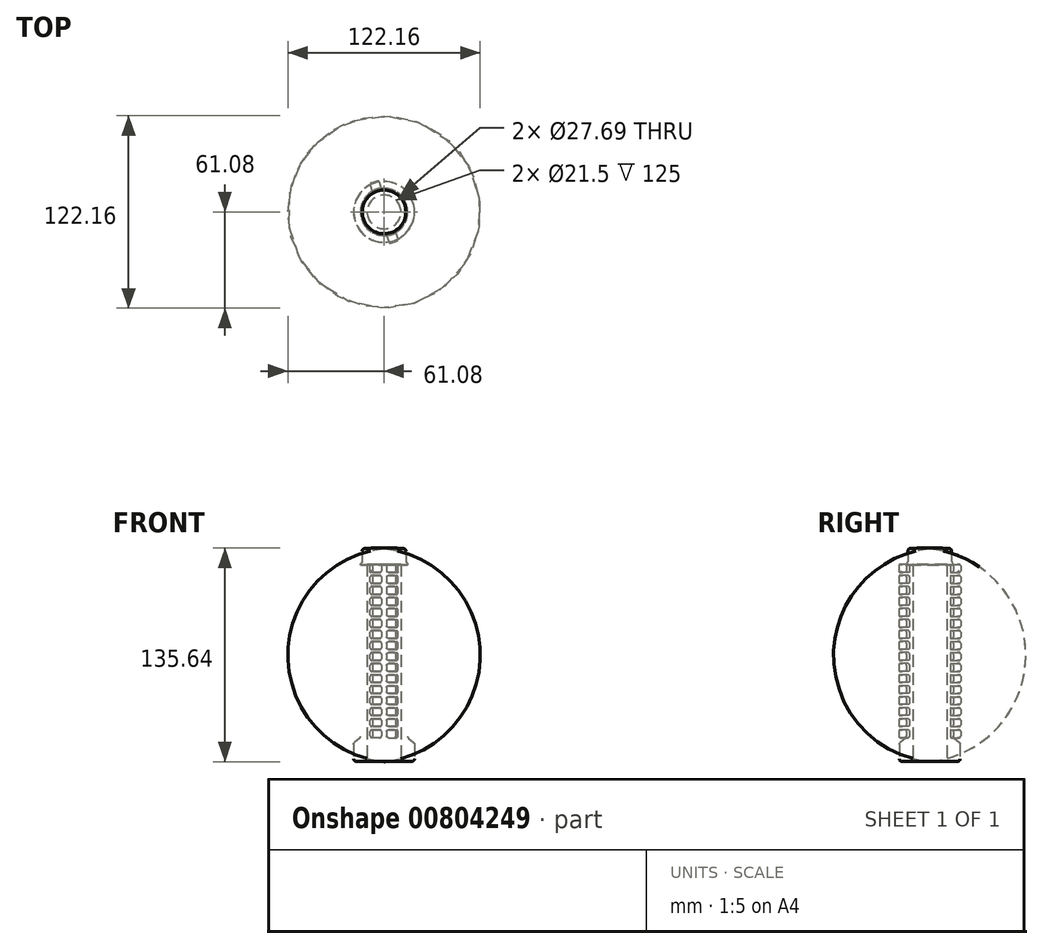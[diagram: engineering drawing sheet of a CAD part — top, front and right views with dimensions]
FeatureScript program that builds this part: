
annotation { "Feature Type Name" : "Feature", "Feature Type Description" : "" }
export const myFeature = defineFeature(function(context is Context, id is Id, definition is map)
    precondition{}
    {
        {
            var Q0;
            Q0=qCreatedBy(makeId("Front.planeOp"),FACE);
            var sketch = newSketch(context, id + "F0", { "sketchPlane" : qUnion([Q0])});
            skLineSegment(sketch, "E0", {"start": v(0, 0) * mm, "end": v(0, 125) * mm, "construction": true});
            skLineSegment(sketch, "E1", {"start": v(0, 135) * mm, "end": v(0, 125) * mm});
            skLineSegment(sketch, "E2", {"start": v(0, 125) * mm, "end": v(10.75, 125) * mm});
            skLineSegment(sketch, "E3", {"start": v(10.75, 125) * mm, "end": v(10.75, 0) * mm});
            skLineSegment(sketch, "E4", {"start": v(10.75, 0) * mm, "end": v(19.33, 0) * mm});
            skLineSegment(sketch, "E5", {"start": v(19.33, 0) * mm, "end": v(19.33, 11.37) * mm});
            skLineSegment(sketch, "E6", {"start": v(19.33, 11.37) * mm, "end": v(15, 15) * mm});
            skLineSegment(sketch, "E7", {"start": v(15, 15) * mm, "end": v(15, 125) * mm});
            skLineSegment(sketch, "E8", {"start": v(15, 125) * mm, "end": v(13.85, 127) * mm});
            skLineSegment(sketch, "E9", {"start": v(13.85, 127) * mm, "end": v(13.85, 135) * mm});
            skArc(sketch, "E10", {"start": v(13.85, 135) * mm, "mid": v(6.92, 135.35) * mm, "end": v(0, 135) * mm});
            skSolve(sketch);
        }
        {
            var Q0;
            Q0 = qSketchRegion(id + "F0", true);
            var Q1;
            Q1=sQuery(id+"F0.wireOp",EDGE,"E0");
            revolve(context, id + "F1", {"surfaceOperationType" : NewSurfaceOperationType.NEW, "entities" : qUnion([Q0]), "axis" : qUnion([Q1]), "revolveType" : RevolveType.FULL});
        }
        {
            var Q0;
            Q0=makeQuery(id+"F1.opRevolve","SWEPT_EDGE",EDGE,{"disambiguationData":[OSD([sQuery(id+"F0.wireOp",EDGE,"E9"),sQuery(id+"F0.wireOp",EDGE,"E10")])]});
            var Q1;
            Q1=makeQuery(id+"F1.opRevolve","SWEPT_EDGE",EDGE,{"disambiguationData":[OSD([sQuery(id+"F0.wireOp",EDGE,"E8"),sQuery(id+"F0.wireOp",EDGE,"E9")])]});
            var Q2;
            Q2=makeQuery(id+"F1.opRevolve","SWEPT_EDGE",EDGE,{"disambiguationData":[OSD([sQuery(id+"F0.wireOp",EDGE,"E7"),sQuery(id+"F0.wireOp",EDGE,"E8")])]});
            var Q3;
            Q3=makeQuery(id+"F1.opRevolve","SWEPT_EDGE",EDGE,{"disambiguationData":[OSD([sQuery(id+"F0.wireOp",EDGE,"E6"),sQuery(id+"F0.wireOp",EDGE,"E7")])]});
            var Q4;
            Q4=makeQuery(id+"F1.opRevolve","SWEPT_EDGE",EDGE,{"disambiguationData":[OSD([sQuery(id+"F0.wireOp",EDGE,"E5"),sQuery(id+"F0.wireOp",EDGE,"E6")])]});
            var Q5;
            Q5=makeQuery(id+"F1.opRevolve","SWEPT_EDGE",EDGE,{"disambiguationData":[OSD([sQuery(id+"F0.wireOp",EDGE,"E4"),sQuery(id+"F0.wireOp",EDGE,"E5")])]});
            fillet(context, id + "F2", {"entities" : qUnion([Q0, Q1, Q2, Q3, Q4, Q5]), "radius" : 1.6 * mm, "tangentPropagation" : true, "allowEdgeOverflow" : false});
        }
        {
            var Q0;
            Q0=qCreatedBy(makeId("Right.planeOp"),FACE);
            cPlane(context, id + "F3", {"entities" : qUnion([Q0]), "cplaneType" : CPlaneType.OFFSET, "offset" : 20 * mm, "width" : 150 * mm, "height" : 150 * mm});
        }
        {
            var Q0;
            Q0=qCreatedBy(id+"F3.planeOp",FACE);
            var sketch = newSketch(context, id + "F4", { "sketchPlane" : qUnion([Q0])});
            skLineSegment(sketch, "E11.bottom", {"start": v(-3, 20) * mm, "end": v(3, 20) * mm});
            skLineSegment(sketch, "E11.top", {"start": v(-3, 15) * mm, "end": v(3, 15) * mm});
            skLineSegment(sketch, "E11.left", {"start": v(-3, 20) * mm, "end": v(-3, 15) * mm});
            skLineSegment(sketch, "E11.right", {"start": v(3, 20) * mm, "end": v(3, 15) * mm});
            skLineSegment(sketch, "E12.MirrorCS", {"start": v(-3, 22) * mm, "end": v(3, 22) * mm});
            skLineSegment(sketch, "E13.MirrorCS", {"start": v(-3, 22) * mm, "end": v(-3, 27) * mm});
            skLineSegment(sketch, "E14.MirrorCS", {"start": v(3, 22) * mm, "end": v(3, 27) * mm});
            skLineSegment(sketch, "E15.MirrorCS", {"start": v(-3, 27) * mm, "end": v(3, 27) * mm});
            skLineSegment(sketch, "E16.MirrorCS", {"start": v(-3, 34) * mm, "end": v(-3, 29) * mm});
            skLineSegment(sketch, "E17.MirrorCS", {"start": v(-3, 29) * mm, "end": v(3, 29) * mm});
            skLineSegment(sketch, "E18.MirrorCS", {"start": v(3, 34) * mm, "end": v(3, 29) * mm});
            skLineSegment(sketch, "E19.MirrorCS", {"start": v(-3, 34) * mm, "end": v(3, 34) * mm});
            skLineSegment(sketch, "E20.MirrorCS", {"start": v(-3, 36) * mm, "end": v(-3, 41) * mm});
            skLineSegment(sketch, "E21.MirrorCS", {"start": v(-3, 41) * mm, "end": v(3, 41) * mm});
            skLineSegment(sketch, "E22.MirrorCS", {"start": v(3, 36) * mm, "end": v(3, 41) * mm});
            skLineSegment(sketch, "E23.MirrorCS", {"start": v(-3, 36) * mm, "end": v(3, 36) * mm});
            skLineSegment(sketch, "E24.MirrorCS", {"start": v(-3, 48) * mm, "end": v(-3, 43) * mm});
            skLineSegment(sketch, "E25.MirrorCS", {"start": v(-3, 48) * mm, "end": v(3, 48) * mm});
            skLineSegment(sketch, "E26.MirrorCS", {"start": v(3, 48) * mm, "end": v(3, 43) * mm});
            skLineSegment(sketch, "E27.MirrorCS", {"start": v(-3, 43) * mm, "end": v(3, 43) * mm});
            skLineSegment(sketch, "E28.MirrorCS", {"start": v(-3, 50) * mm, "end": v(3, 50) * mm});
            skLineSegment(sketch, "E29.MirrorCS", {"start": v(-3, 50) * mm, "end": v(-3, 55) * mm});
            skLineSegment(sketch, "E30.MirrorCS", {"start": v(-3, 55) * mm, "end": v(3, 55) * mm});
            skLineSegment(sketch, "E31.MirrorCS", {"start": v(3, 50) * mm, "end": v(3, 55) * mm});
            skLineSegment(sketch, "E32.MirrorCS", {"start": v(-3, 62) * mm, "end": v(-3, 57) * mm});
            skLineSegment(sketch, "E33.MirrorCS", {"start": v(-3, 62) * mm, "end": v(3, 62) * mm});
            skLineSegment(sketch, "E34.MirrorCS", {"start": v(3, 62) * mm, "end": v(3, 57) * mm});
            skLineSegment(sketch, "E35.MirrorCS", {"start": v(-3, 57) * mm, "end": v(3, 57) * mm});
            skLineSegment(sketch, "E36.MirrorCS", {"start": v(3, 92) * mm, "end": v(3, 97) * mm});
            skLineSegment(sketch, "E37.MirrorCS", {"start": v(-3, 97) * mm, "end": v(3, 97) * mm});
            skLineSegment(sketch, "E38.MirrorCS", {"start": v(-3, 92) * mm, "end": v(-3, 97) * mm});
            skLineSegment(sketch, "E39.MirrorCS", {"start": v(-3, 92) * mm, "end": v(3, 92) * mm});
            skLineSegment(sketch, "E40.MirrorCS", {"start": v(-3, 85) * mm, "end": v(3, 85) * mm});
            skLineSegment(sketch, "E41.MirrorCS", {"start": v(-3, 90) * mm, "end": v(-3, 85) * mm});
            skLineSegment(sketch, "E42.MirrorCS", {"start": v(3, 90) * mm, "end": v(3, 85) * mm});
            skLineSegment(sketch, "E43.MirrorCS", {"start": v(-3, 83) * mm, "end": v(3, 83) * mm});
            skLineSegment(sketch, "E44.MirrorCS", {"start": v(-3, 78) * mm, "end": v(-3, 83) * mm});
            skLineSegment(sketch, "E45.MirrorCS", {"start": v(3, 78) * mm, "end": v(3, 83) * mm});
            skLineSegment(sketch, "E46.MirrorCS", {"start": v(-3, 78) * mm, "end": v(3, 78) * mm});
            skLineSegment(sketch, "E47.MirrorCS", {"start": v(-3, 76) * mm, "end": v(3, 76) * mm});
            skLineSegment(sketch, "E48.MirrorCS", {"start": v(3, 76) * mm, "end": v(3, 71) * mm});
            skLineSegment(sketch, "E49.MirrorCS", {"start": v(-3, 76) * mm, "end": v(-3, 71) * mm});
            skLineSegment(sketch, "E50.MirrorCS", {"start": v(-3, 71) * mm, "end": v(3, 71) * mm});
            skLineSegment(sketch, "E51.MirrorCS", {"start": v(-3, 69) * mm, "end": v(3, 69) * mm});
            skLineSegment(sketch, "E52.MirrorCS", {"start": v(3, 64) * mm, "end": v(3, 69) * mm});
            skLineSegment(sketch, "E53.MirrorCS", {"start": v(-3, 64) * mm, "end": v(-3, 69) * mm});
            skLineSegment(sketch, "E54.MirrorCS", {"start": v(-3, 64) * mm, "end": v(3, 64) * mm});
            skLineSegment(sketch, "E55", {"start": v(-3, 90) * mm, "end": v(3, 90) * mm});
            skLineSegment(sketch, "E56.MirrorCS", {"start": v(-3, 125) * mm, "end": v(3, 125) * mm});
            skLineSegment(sketch, "E57.MirrorCS", {"start": v(-3, 120) * mm, "end": v(-3, 125) * mm});
            skLineSegment(sketch, "E58.MirrorCS", {"start": v(-3, 120) * mm, "end": v(3, 120) * mm});
            skLineSegment(sketch, "E59.MirrorCS", {"start": v(3, 120) * mm, "end": v(3, 125) * mm});
            skLineSegment(sketch, "E60.MirrorCS", {"start": v(-3, 118) * mm, "end": v(3, 118) * mm});
            skLineSegment(sketch, "E61.MirrorCS", {"start": v(-3, 118) * mm, "end": v(-3, 113) * mm});
            skLineSegment(sketch, "E62.MirrorCS", {"start": v(-3, 113) * mm, "end": v(3, 113) * mm});
            skLineSegment(sketch, "E63.MirrorCS", {"start": v(3, 118) * mm, "end": v(3, 113) * mm});
            skLineSegment(sketch, "E64.MirrorCS", {"start": v(-3, 111) * mm, "end": v(3, 111) * mm});
            skLineSegment(sketch, "E65.MirrorCS", {"start": v(-3, 106) * mm, "end": v(-3, 111) * mm});
            skLineSegment(sketch, "E66.MirrorCS", {"start": v(-3, 106) * mm, "end": v(3, 106) * mm});
            skLineSegment(sketch, "E67.MirrorCS", {"start": v(3, 106) * mm, "end": v(3, 111) * mm});
            skLineSegment(sketch, "E68.MirrorCS", {"start": v(-3, 104) * mm, "end": v(3, 104) * mm});
            skLineSegment(sketch, "E69.MirrorCS", {"start": v(3, 104) * mm, "end": v(3, 99) * mm});
            skLineSegment(sketch, "E70.MirrorCS", {"start": v(-3, 99) * mm, "end": v(3, 99) * mm});
            skLineSegment(sketch, "E71.MirrorCS", {"start": v(-3, 104) * mm, "end": v(-3, 99) * mm});
            skSolve(sketch);
        }
        {
            var Q0;
            Q0 = qSketchRegion(id + "F4", true);
            var Q1;
            Q1=makeQuery(id+"F1.opRevolve","SWEPT_FACE",FACE,{"disambiguationData":[OSD([sQuery(id+"F0.wireOp",EDGE,"E7")])]});
            extrude(context, id + "F5", {"entities" : qUnion([Q0]), "operationType" : NewBodyOperationType.ADD, "endBound" : BoundingType.UP_TO_SURFACE, "oppositeDirection" : true, "depth" : 25 * mm, "endBoundEntityFace" : qUnion([Q1]), "offsetDistance" : 25 * mm});
        }
        {
            var Q0;
            Q0=makeQuery(id+"F5.opExtrude","CAP_EDGE",EDGE,{"disambiguationData":[OSD([sQuery(id+"F4.wireOp",EDGE,"E11.right")])],"isStart":true});
            var Q1;
            Q1=makeQuery(id+"F5.opExtrude","SWEPT_EDGE",EDGE,{"disambiguationData":[OSD([sQuery(id+"F4.wireOp",EDGE,"E11.bottom"),sQuery(id+"F4.wireOp",EDGE,"E11.right")])]});
            var Q2;
            Q2=makeQuery(id+"F5.opExtrude","SWEPT_EDGE",EDGE,{"disambiguationData":[OSD([sQuery(id+"F4.wireOp",EDGE,"E11.bottom"),sQuery(id+"F4.wireOp",EDGE,"E11.left")])]});
            var Q3;
            Q3=makeQuery(id+"F5.opExtrude","CAP_EDGE",EDGE,{"disambiguationData":[OSD([sQuery(id+"F4.wireOp",EDGE,"E11.left")])],"isStart":true});
            var Q4;
            Q4=makeQuery(id+"F5.opExtrude","CAP_EDGE",EDGE,{"disambiguationData":[OSD([sQuery(id+"F4.wireOp",EDGE,"E11.bottom")])],"isStart":true});
            var Q5;
            Q5=makeQuery(id+"F5.opExtrude","CAP_EDGE",EDGE,{"disambiguationData":[OSD([sQuery(id+"F4.wireOp",EDGE,"E11.top")])],"isStart":true});
            var Q6;
            Q6=makeQuery(id+"F5.opExtrude","SWEPT_EDGE",EDGE,{"disambiguationData":[OSD([sQuery(id+"F4.wireOp",EDGE,"E11.top"),sQuery(id+"F4.wireOp",EDGE,"E11.left")])]});
            var Q7;
            Q7=makeQuery(id+"F5.opExtrude","SWEPT_EDGE",EDGE,{"disambiguationData":[OSD([sQuery(id+"F4.wireOp",EDGE,"E16.MirrorCS"),sQuery(id+"F4.wireOp",EDGE,"E19.MirrorCS")])]});
            var Q8;
            Q8=makeQuery(id+"F5.opExtrude","SWEPT_EDGE",EDGE,{"disambiguationData":[OSD([sQuery(id+"F4.wireOp",EDGE,"E16.MirrorCS"),sQuery(id+"F4.wireOp",EDGE,"E17.MirrorCS")])]});
            var Q9;
            Q9=makeQuery(id+"F5.opExtrude","SWEPT_EDGE",EDGE,{"disambiguationData":[OSD([sQuery(id+"F4.wireOp",EDGE,"E13.MirrorCS"),sQuery(id+"F4.wireOp",EDGE,"E15.MirrorCS")])]});
            var Q10;
            Q10=makeQuery(id+"F5.opExtrude","SWEPT_EDGE",EDGE,{"disambiguationData":[OSD([sQuery(id+"F4.wireOp",EDGE,"E12.MirrorCS"),sQuery(id+"F4.wireOp",EDGE,"E13.MirrorCS")])]});
            var Q11;
            Q11=makeQuery(id+"F5.opExtrude","CAP_EDGE",EDGE,{"disambiguationData":[OSD([sQuery(id+"F4.wireOp",EDGE,"E15.MirrorCS")])],"isStart":true});
            var Q12;
            Q12=makeQuery(id+"F5.opExtrude","CAP_EDGE",EDGE,{"disambiguationData":[OSD([sQuery(id+"F4.wireOp",EDGE,"E12.MirrorCS")])],"isStart":true});
            var Q13;
            Q13=makeQuery(id+"F5.opExtrude","CAP_EDGE",EDGE,{"disambiguationData":[OSD([sQuery(id+"F4.wireOp",EDGE,"E14.MirrorCS")])],"isStart":true});
            var Q14;
            Q14=makeQuery(id+"F5.opExtrude","CAP_EDGE",EDGE,{"disambiguationData":[OSD([sQuery(id+"F4.wireOp",EDGE,"E17.MirrorCS")])],"isStart":true});
            var Q15;
            Q15=makeQuery(id+"F5.opExtrude","CAP_EDGE",EDGE,{"disambiguationData":[OSD([sQuery(id+"F4.wireOp",EDGE,"E19.MirrorCS")])],"isStart":true});
            var Q16;
            Q16=makeQuery(id+"F5.opExtrude","CAP_EDGE",EDGE,{"disambiguationData":[OSD([sQuery(id+"F4.wireOp",EDGE,"E16.MirrorCS")])],"isStart":true});
            var Q17;
            Q17=makeQuery(id+"F5.opExtrude","CAP_EDGE",EDGE,{"disambiguationData":[OSD([sQuery(id+"F4.wireOp",EDGE,"E18.MirrorCS")])],"isStart":true});
            var Q18;
            Q18=makeQuery(id+"F5.opExtrude","CAP_EDGE",EDGE,{"disambiguationData":[OSD([sQuery(id+"F4.wireOp",EDGE,"E22.MirrorCS")])],"isStart":true});
            var Q19;
            Q19=makeQuery(id+"F5.opExtrude","CAP_EDGE",EDGE,{"disambiguationData":[OSD([sQuery(id+"F4.wireOp",EDGE,"E23.MirrorCS")])],"isStart":true});
            var Q20;
            Q20=makeQuery(id+"F5.opExtrude","CAP_EDGE",EDGE,{"disambiguationData":[OSD([sQuery(id+"F4.wireOp",EDGE,"E21.MirrorCS")])],"isStart":true});
            var Q21;
            Q21=makeQuery(id+"F5.opExtrude","CAP_EDGE",EDGE,{"disambiguationData":[OSD([sQuery(id+"F4.wireOp",EDGE,"E20.MirrorCS")])],"isStart":true});
            var Q22;
            Q22=makeQuery(id+"F5.opExtrude","SWEPT_EDGE",EDGE,{"disambiguationData":[OSD([sQuery(id+"F4.wireOp",EDGE,"E20.MirrorCS"),sQuery(id+"F4.wireOp",EDGE,"E23.MirrorCS")])]});
            var Q23;
            Q23=makeQuery(id+"F5.opExtrude","SWEPT_EDGE",EDGE,{"disambiguationData":[OSD([sQuery(id+"F4.wireOp",EDGE,"E20.MirrorCS"),sQuery(id+"F4.wireOp",EDGE,"E21.MirrorCS")])]});
            var Q24;
            Q24=makeQuery(id+"F5.opExtrude","SWEPT_EDGE",EDGE,{"disambiguationData":[OSD([sQuery(id+"F4.wireOp",EDGE,"E24.MirrorCS"),sQuery(id+"F4.wireOp",EDGE,"E25.MirrorCS")])]});
            var Q25;
            Q25=makeQuery(id+"F5.opExtrude","SWEPT_EDGE",EDGE,{"disambiguationData":[OSD([sQuery(id+"F4.wireOp",EDGE,"E24.MirrorCS"),sQuery(id+"F4.wireOp",EDGE,"E27.MirrorCS")])]});
            var Q26;
            Q26=makeQuery(id+"F5.opExtrude","CAP_EDGE",EDGE,{"disambiguationData":[OSD([sQuery(id+"F4.wireOp",EDGE,"E24.MirrorCS")])],"isStart":true});
            var Q27;
            Q27=makeQuery(id+"F5.opExtrude","CAP_EDGE",EDGE,{"disambiguationData":[OSD([sQuery(id+"F4.wireOp",EDGE,"E27.MirrorCS")])],"isStart":true});
            var Q28;
            Q28=makeQuery(id+"F5.opExtrude","CAP_EDGE",EDGE,{"disambiguationData":[OSD([sQuery(id+"F4.wireOp",EDGE,"E25.MirrorCS")])],"isStart":true});
            var Q29;
            Q29=makeQuery(id+"F5.opExtrude","CAP_EDGE",EDGE,{"disambiguationData":[OSD([sQuery(id+"F4.wireOp",EDGE,"E26.MirrorCS")])],"isStart":true});
            var Q30;
            Q30=makeQuery(id+"F5.opExtrude","SWEPT_EDGE",EDGE,{"disambiguationData":[OSD([sQuery(id+"F4.wireOp",EDGE,"E28.MirrorCS"),sQuery(id+"F4.wireOp",EDGE,"E29.MirrorCS")])]});
            var Q31;
            Q31=makeQuery(id+"F5.opExtrude","SWEPT_EDGE",EDGE,{"disambiguationData":[OSD([sQuery(id+"F4.wireOp",EDGE,"E29.MirrorCS"),sQuery(id+"F4.wireOp",EDGE,"E30.MirrorCS")])]});
            var Q32;
            Q32=makeQuery(id+"F5.opExtrude","CAP_EDGE",EDGE,{"disambiguationData":[OSD([sQuery(id+"F4.wireOp",EDGE,"E30.MirrorCS")])],"isStart":true});
            var Q33;
            Q33=makeQuery(id+"F5.opExtrude","CAP_EDGE",EDGE,{"disambiguationData":[OSD([sQuery(id+"F4.wireOp",EDGE,"E28.MirrorCS")])],"isStart":true});
            var Q34;
            Q34=makeQuery(id+"F5.opExtrude","CAP_EDGE",EDGE,{"disambiguationData":[OSD([sQuery(id+"F4.wireOp",EDGE,"E31.MirrorCS")])],"isStart":true});
            var Q35;
            Q35=makeQuery(id+"F5.opExtrude","CAP_EDGE",EDGE,{"disambiguationData":[OSD([sQuery(id+"F4.wireOp",EDGE,"E29.MirrorCS")])],"isStart":true});
            var Q36;
            Q36=makeQuery(id+"F5.opExtrude","CAP_EDGE",EDGE,{"disambiguationData":[OSD([sQuery(id+"F4.wireOp",EDGE,"E53.MirrorCS")])],"isStart":true});
            var Q37;
            Q37=makeQuery(id+"F5.opExtrude","SWEPT_EDGE",EDGE,{"disambiguationData":[OSD([sQuery(id+"F4.wireOp",EDGE,"E51.MirrorCS"),sQuery(id+"F4.wireOp",EDGE,"E53.MirrorCS")])]});
            var Q38;
            Q38=makeQuery(id+"F5.opExtrude","SWEPT_EDGE",EDGE,{"disambiguationData":[OSD([sQuery(id+"F4.wireOp",EDGE,"E53.MirrorCS"),sQuery(id+"F4.wireOp",EDGE,"E54.MirrorCS")])]});
            var Q39;
            Q39=makeQuery(id+"F5.opExtrude","CAP_EDGE",EDGE,{"disambiguationData":[OSD([sQuery(id+"F4.wireOp",EDGE,"E51.MirrorCS")])],"isStart":true});
            var Q40;
            Q40=makeQuery(id+"F5.opExtrude","CAP_EDGE",EDGE,{"disambiguationData":[OSD([sQuery(id+"F4.wireOp",EDGE,"E54.MirrorCS")])],"isStart":true});
            var Q41;
            Q41=makeQuery(id+"F5.opExtrude","CAP_EDGE",EDGE,{"disambiguationData":[OSD([sQuery(id+"F4.wireOp",EDGE,"E52.MirrorCS")])],"isStart":true});
            var Q42;
            Q42=makeQuery(id+"F5.opExtrude","CAP_EDGE",EDGE,{"disambiguationData":[OSD([sQuery(id+"F4.wireOp",EDGE,"E48.MirrorCS")])],"isStart":true});
            var Q43;
            Q43=makeQuery(id+"F5.opExtrude","CAP_EDGE",EDGE,{"disambiguationData":[OSD([sQuery(id+"F4.wireOp",EDGE,"E50.MirrorCS")])],"isStart":true});
            var Q44;
            Q44=makeQuery(id+"F5.opExtrude","CAP_EDGE",EDGE,{"disambiguationData":[OSD([sQuery(id+"F4.wireOp",EDGE,"E47.MirrorCS")])],"isStart":true});
            var Q45;
            Q45=makeQuery(id+"F5.opExtrude","SWEPT_EDGE",EDGE,{"disambiguationData":[OSD([sQuery(id+"F4.wireOp",EDGE,"E47.MirrorCS"),sQuery(id+"F4.wireOp",EDGE,"E49.MirrorCS")])]});
            var Q46;
            Q46=makeQuery(id+"F5.opExtrude","SWEPT_EDGE",EDGE,{"disambiguationData":[OSD([sQuery(id+"F4.wireOp",EDGE,"E49.MirrorCS"),sQuery(id+"F4.wireOp",EDGE,"E50.MirrorCS")])]});
            var Q47;
            Q47=makeQuery(id+"F5.opExtrude","CAP_EDGE",EDGE,{"disambiguationData":[OSD([sQuery(id+"F4.wireOp",EDGE,"E49.MirrorCS")])],"isStart":true});
            var Q48;
            Q48=makeQuery(id+"F5.opExtrude","SWEPT_EDGE",EDGE,{"disambiguationData":[OSD([sQuery(id+"F4.wireOp",EDGE,"E32.MirrorCS"),sQuery(id+"F4.wireOp",EDGE,"E33.MirrorCS")])]});
            var Q49;
            Q49=makeQuery(id+"F5.opExtrude","SWEPT_EDGE",EDGE,{"disambiguationData":[OSD([sQuery(id+"F4.wireOp",EDGE,"E32.MirrorCS"),sQuery(id+"F4.wireOp",EDGE,"E35.MirrorCS")])]});
            var Q50;
            Q50=makeQuery(id+"F5.opExtrude","CAP_EDGE",EDGE,{"disambiguationData":[OSD([sQuery(id+"F4.wireOp",EDGE,"E32.MirrorCS")])],"isStart":true});
            var Q51;
            Q51=makeQuery(id+"F5.opExtrude","CAP_EDGE",EDGE,{"disambiguationData":[OSD([sQuery(id+"F4.wireOp",EDGE,"E33.MirrorCS")])],"isStart":true});
            var Q52;
            Q52=makeQuery(id+"F5.opExtrude","CAP_EDGE",EDGE,{"disambiguationData":[OSD([sQuery(id+"F4.wireOp",EDGE,"E34.MirrorCS")])],"isStart":true});
            var Q53;
            Q53=makeQuery(id+"F5.opExtrude","CAP_FACE",FACE,{"disambiguationData":[OSD([sQuery(id+"F4.wireOp",EDGE,"E32.MirrorCS"),sQuery(id+"F4.wireOp",EDGE,"E33.MirrorCS"),sQuery(id+"F4.wireOp",EDGE,"E34.MirrorCS"),sQuery(id+"F4.wireOp",EDGE,"E35.MirrorCS")])],"isStart":true});
            var Q54;
            Q54=makeQuery(id+"F5.opExtrude","CAP_EDGE",EDGE,{"disambiguationData":[OSD([sQuery(id+"F4.wireOp",EDGE,"E46.MirrorCS")])],"isStart":true});
            var Q55;
            Q55=makeQuery(id+"F5.opExtrude","CAP_EDGE",EDGE,{"disambiguationData":[OSD([sQuery(id+"F4.wireOp",EDGE,"E45.MirrorCS")])],"isStart":true});
            var Q56;
            Q56=makeQuery(id+"F5.opExtrude","CAP_EDGE",EDGE,{"disambiguationData":[OSD([sQuery(id+"F4.wireOp",EDGE,"E43.MirrorCS")])],"isStart":true});
            var Q57;
            Q57=makeQuery(id+"F5.opExtrude","CAP_EDGE",EDGE,{"disambiguationData":[OSD([sQuery(id+"F4.wireOp",EDGE,"E44.MirrorCS")])],"isStart":true});
            var Q58;
            Q58=makeQuery(id+"F5.opExtrude","SWEPT_EDGE",EDGE,{"disambiguationData":[OSD([sQuery(id+"F4.wireOp",EDGE,"E43.MirrorCS"),sQuery(id+"F4.wireOp",EDGE,"E44.MirrorCS")])]});
            var Q59;
            Q59=makeQuery(id+"F5.opExtrude","SWEPT_EDGE",EDGE,{"disambiguationData":[OSD([sQuery(id+"F4.wireOp",EDGE,"E44.MirrorCS"),sQuery(id+"F4.wireOp",EDGE,"E46.MirrorCS")])]});
            var Q60;
            Q60=makeQuery(id+"F5.opExtrude","SWEPT_EDGE",EDGE,{"disambiguationData":[OSD([sQuery(id+"F4.wireOp",EDGE,"E55"),sQuery(id+"F4.wireOp",EDGE,"E41.MirrorCS")])]});
            var Q61;
            Q61=makeQuery(id+"F5.opExtrude","CAP_EDGE",EDGE,{"disambiguationData":[OSD([sQuery(id+"F4.wireOp",EDGE,"E55")])],"isStart":true});
            var Q62;
            Q62=makeQuery(id+"F5.opExtrude","CAP_EDGE",EDGE,{"disambiguationData":[OSD([sQuery(id+"F4.wireOp",EDGE,"E42.MirrorCS")])],"isStart":true});
            var Q63;
            Q63=makeQuery(id+"F5.opExtrude","CAP_EDGE",EDGE,{"disambiguationData":[OSD([sQuery(id+"F4.wireOp",EDGE,"E40.MirrorCS")])],"isStart":true});
            var Q64;
            Q64=makeQuery(id+"F5.opExtrude","SWEPT_EDGE",EDGE,{"disambiguationData":[OSD([sQuery(id+"F4.wireOp",EDGE,"E41.MirrorCS"),sQuery(id+"F4.wireOp",EDGE,"E40.MirrorCS")])]});
            var Q65;
            Q65=makeQuery(id+"F5.opExtrude","CAP_EDGE",EDGE,{"disambiguationData":[OSD([sQuery(id+"F4.wireOp",EDGE,"E41.MirrorCS")])],"isStart":true});
            var Q66;
            Q66=makeQuery(id+"F5.opExtrude","SWEPT_EDGE",EDGE,{"disambiguationData":[OSD([sQuery(id+"F4.wireOp",EDGE,"E37.MirrorCS"),sQuery(id+"F4.wireOp",EDGE,"E38.MirrorCS")])]});
            var Q67;
            Q67=makeQuery(id+"F5.opExtrude","SWEPT_EDGE",EDGE,{"disambiguationData":[OSD([sQuery(id+"F4.wireOp",EDGE,"E39.MirrorCS"),sQuery(id+"F4.wireOp",EDGE,"E38.MirrorCS")])]});
            var Q68;
            Q68=makeQuery(id+"F5.opExtrude","CAP_EDGE",EDGE,{"disambiguationData":[OSD([sQuery(id+"F4.wireOp",EDGE,"E38.MirrorCS")])],"isStart":true});
            var Q69;
            Q69=makeQuery(id+"F5.opExtrude","CAP_EDGE",EDGE,{"disambiguationData":[OSD([sQuery(id+"F4.wireOp",EDGE,"E37.MirrorCS")])],"isStart":true});
            var Q70;
            Q70=makeQuery(id+"F5.opExtrude","CAP_EDGE",EDGE,{"disambiguationData":[OSD([sQuery(id+"F4.wireOp",EDGE,"E36.MirrorCS")])],"isStart":true});
            var Q71;
            Q71=makeQuery(id+"F5.opExtrude","CAP_EDGE",EDGE,{"disambiguationData":[OSD([sQuery(id+"F4.wireOp",EDGE,"E39.MirrorCS")])],"isStart":true});
            var Q72;
            Q72=makeQuery(id+"F5.opExtrude","SWEPT_EDGE",EDGE,{"disambiguationData":[OSD([sQuery(id+"F4.wireOp",EDGE,"E68.MirrorCS"),sQuery(id+"F4.wireOp",EDGE,"E71.MirrorCS")])]});
            var Q73;
            Q73=makeQuery(id+"F5.opExtrude","CAP_EDGE",EDGE,{"disambiguationData":[OSD([sQuery(id+"F4.wireOp",EDGE,"E70.MirrorCS")])],"isStart":true});
            var Q74;
            Q74=makeQuery(id+"F5.opExtrude","CAP_EDGE",EDGE,{"disambiguationData":[OSD([sQuery(id+"F4.wireOp",EDGE,"E71.MirrorCS")])],"isStart":true});
            var Q75;
            Q75=makeQuery(id+"F5.opExtrude","CAP_EDGE",EDGE,{"disambiguationData":[OSD([sQuery(id+"F4.wireOp",EDGE,"E68.MirrorCS")])],"isStart":true});
            var Q76;
            Q76=makeQuery(id+"F5.opExtrude","SWEPT_EDGE",EDGE,{"disambiguationData":[OSD([sQuery(id+"F4.wireOp",EDGE,"E70.MirrorCS"),sQuery(id+"F4.wireOp",EDGE,"E71.MirrorCS")])]});
            var Q77;
            Q77=makeQuery(id+"F5.opExtrude","CAP_EDGE",EDGE,{"disambiguationData":[OSD([sQuery(id+"F4.wireOp",EDGE,"E69.MirrorCS")])],"isStart":true});
            var Q78;
            Q78=makeQuery(id+"F5.opExtrude","CAP_EDGE",EDGE,{"disambiguationData":[OSD([sQuery(id+"F4.wireOp",EDGE,"E67.MirrorCS")])],"isStart":true});
            var Q79;
            Q79=makeQuery(id+"F5.opExtrude","CAP_EDGE",EDGE,{"disambiguationData":[OSD([sQuery(id+"F4.wireOp",EDGE,"E64.MirrorCS")])],"isStart":true});
            var Q80;
            Q80=makeQuery(id+"F5.opExtrude","CAP_EDGE",EDGE,{"disambiguationData":[OSD([sQuery(id+"F4.wireOp",EDGE,"E66.MirrorCS")])],"isStart":true});
            var Q81;
            Q81=makeQuery(id+"F5.opExtrude","CAP_EDGE",EDGE,{"disambiguationData":[OSD([sQuery(id+"F4.wireOp",EDGE,"E65.MirrorCS")])],"isStart":true});
            var Q82;
            Q82=makeQuery(id+"F5.opExtrude","SWEPT_EDGE",EDGE,{"disambiguationData":[OSD([sQuery(id+"F4.wireOp",EDGE,"E64.MirrorCS"),sQuery(id+"F4.wireOp",EDGE,"E65.MirrorCS")])]});
            var Q83;
            Q83=makeQuery(id+"F5.opExtrude","SWEPT_EDGE",EDGE,{"disambiguationData":[OSD([sQuery(id+"F4.wireOp",EDGE,"E65.MirrorCS"),sQuery(id+"F4.wireOp",EDGE,"E66.MirrorCS")])]});
            var Q84;
            Q84=makeQuery(id+"F5.opExtrude","SWEPT_EDGE",EDGE,{"disambiguationData":[OSD([sQuery(id+"F4.wireOp",EDGE,"E61.MirrorCS"),sQuery(id+"F4.wireOp",EDGE,"E62.MirrorCS")])]});
            var Q85;
            Q85=makeQuery(id+"F5.opExtrude","SWEPT_EDGE",EDGE,{"disambiguationData":[OSD([sQuery(id+"F4.wireOp",EDGE,"E61.MirrorCS"),sQuery(id+"F4.wireOp",EDGE,"E60.MirrorCS")])]});
            var Q86;
            Q86=makeQuery(id+"F5.opExtrude","CAP_EDGE",EDGE,{"disambiguationData":[OSD([sQuery(id+"F4.wireOp",EDGE,"E60.MirrorCS")])],"isStart":true});
            var Q87;
            Q87=makeQuery(id+"F5.opExtrude","CAP_EDGE",EDGE,{"disambiguationData":[OSD([sQuery(id+"F4.wireOp",EDGE,"E62.MirrorCS")])],"isStart":true});
            var Q88;
            Q88=makeQuery(id+"F5.opExtrude","CAP_EDGE",EDGE,{"disambiguationData":[OSD([sQuery(id+"F4.wireOp",EDGE,"E63.MirrorCS")])],"isStart":true});
            var Q89;
            Q89=makeQuery(id+"F5.opExtrude","CAP_EDGE",EDGE,{"disambiguationData":[OSD([sQuery(id+"F4.wireOp",EDGE,"E61.MirrorCS")])],"isStart":true});
            var Q90;
            Q90=makeQuery(id+"F5.opExtrude","SWEPT_EDGE",EDGE,{"disambiguationData":[OSD([sQuery(id+"F4.wireOp",EDGE,"E56.MirrorCS"),sQuery(id+"F4.wireOp",EDGE,"E57.MirrorCS")])]});
            var Q91;
            Q91=makeQuery(id+"F5.opExtrude","CAP_EDGE",EDGE,{"disambiguationData":[OSD([sQuery(id+"F4.wireOp",EDGE,"E57.MirrorCS")])],"isStart":true});
            var Q92;
            Q92=makeQuery(id+"F5.opExtrude","SWEPT_EDGE",EDGE,{"disambiguationData":[OSD([sQuery(id+"F4.wireOp",EDGE,"E57.MirrorCS"),sQuery(id+"F4.wireOp",EDGE,"E58.MirrorCS")])]});
            var Q93;
            Q93=makeQuery(id+"F5.opExtrude","SWEPT_EDGE",EDGE,{"disambiguationData":[OSD([sQuery(id+"F4.wireOp",EDGE,"E56.MirrorCS"),sQuery(id+"F4.wireOp",EDGE,"E59.MirrorCS")])]});
            var Q94;
            Q94=makeQuery(id+"F5.opExtrude","CAP_EDGE",EDGE,{"disambiguationData":[OSD([sQuery(id+"F4.wireOp",EDGE,"E59.MirrorCS")])],"isStart":true});
            var Q95;
            Q95=makeQuery(id+"F5.opExtrude","CAP_EDGE",EDGE,{"disambiguationData":[OSD([sQuery(id+"F4.wireOp",EDGE,"E58.MirrorCS")])],"isStart":true});
            var Q96;
            Q96=makeQuery(id+"F5.opExtrude","CAP_EDGE",EDGE,{"disambiguationData":[OSD([sQuery(id+"F4.wireOp",EDGE,"E56.MirrorCS")])],"isStart":true});
            var Q97;
            Q97=makeQuery(id+"F5.opExtrude","SWEPT_EDGE",EDGE,{"disambiguationData":[OSD([sQuery(id+"F4.wireOp",EDGE,"E63.MirrorCS"),sQuery(id+"F4.wireOp",EDGE,"E60.MirrorCS")])]});
            var Q98;
            Q98=makeQuery(id+"F5.opExtrude","SWEPT_EDGE",EDGE,{"disambiguationData":[OSD([sQuery(id+"F4.wireOp",EDGE,"E62.MirrorCS"),sQuery(id+"F4.wireOp",EDGE,"E63.MirrorCS")])]});
            var Q99;
            Q99=makeQuery(id+"F5.opExtrude","SWEPT_EDGE",EDGE,{"disambiguationData":[OSD([sQuery(id+"F4.wireOp",EDGE,"E64.MirrorCS"),sQuery(id+"F4.wireOp",EDGE,"E67.MirrorCS")])]});
            var Q100;
            Q100=makeQuery(id+"F5.opExtrude","SWEPT_EDGE",EDGE,{"disambiguationData":[OSD([sQuery(id+"F4.wireOp",EDGE,"E66.MirrorCS"),sQuery(id+"F4.wireOp",EDGE,"E67.MirrorCS")])]});
            var Q101;
            Q101=makeQuery(id+"F5.opExtrude","SWEPT_EDGE",EDGE,{"disambiguationData":[OSD([sQuery(id+"F4.wireOp",EDGE,"E68.MirrorCS"),sQuery(id+"F4.wireOp",EDGE,"E69.MirrorCS")])]});
            var Q102;
            Q102=makeQuery(id+"F5.opExtrude","SWEPT_EDGE",EDGE,{"disambiguationData":[OSD([sQuery(id+"F4.wireOp",EDGE,"E69.MirrorCS"),sQuery(id+"F4.wireOp",EDGE,"E70.MirrorCS")])]});
            var Q103;
            Q103=makeQuery(id+"F5.opExtrude","SWEPT_EDGE",EDGE,{"disambiguationData":[OSD([sQuery(id+"F4.wireOp",EDGE,"E36.MirrorCS"),sQuery(id+"F4.wireOp",EDGE,"E37.MirrorCS")])]});
            var Q104;
            Q104=makeQuery(id+"F5.opExtrude","SWEPT_EDGE",EDGE,{"disambiguationData":[OSD([sQuery(id+"F4.wireOp",EDGE,"E36.MirrorCS"),sQuery(id+"F4.wireOp",EDGE,"E39.MirrorCS")])]});
            var Q105;
            Q105=makeQuery(id+"F5.opExtrude","SWEPT_EDGE",EDGE,{"disambiguationData":[OSD([sQuery(id+"F4.wireOp",EDGE,"E55"),sQuery(id+"F4.wireOp",EDGE,"E42.MirrorCS")])]});
            var Q106;
            Q106=makeQuery(id+"F5.opExtrude","SWEPT_EDGE",EDGE,{"disambiguationData":[OSD([sQuery(id+"F4.wireOp",EDGE,"E40.MirrorCS"),sQuery(id+"F4.wireOp",EDGE,"E42.MirrorCS")])]});
            var Q107;
            Q107=makeQuery(id+"F5.opExtrude","SWEPT_EDGE",EDGE,{"disambiguationData":[OSD([sQuery(id+"F4.wireOp",EDGE,"E43.MirrorCS"),sQuery(id+"F4.wireOp",EDGE,"E45.MirrorCS")])]});
            var Q108;
            Q108=makeQuery(id+"F5.opExtrude","SWEPT_EDGE",EDGE,{"disambiguationData":[OSD([sQuery(id+"F4.wireOp",EDGE,"E45.MirrorCS"),sQuery(id+"F4.wireOp",EDGE,"E46.MirrorCS")])]});
            var Q109;
            Q109=makeQuery(id+"F5.opExtrude","SWEPT_EDGE",EDGE,{"disambiguationData":[OSD([sQuery(id+"F4.wireOp",EDGE,"E47.MirrorCS"),sQuery(id+"F4.wireOp",EDGE,"E48.MirrorCS")])]});
            var Q110;
            Q110=makeQuery(id+"F5.opExtrude","SWEPT_EDGE",EDGE,{"disambiguationData":[OSD([sQuery(id+"F4.wireOp",EDGE,"E48.MirrorCS"),sQuery(id+"F4.wireOp",EDGE,"E50.MirrorCS")])]});
            var Q111;
            Q111=makeQuery(id+"F5.opExtrude","SWEPT_EDGE",EDGE,{"disambiguationData":[OSD([sQuery(id+"F4.wireOp",EDGE,"E51.MirrorCS"),sQuery(id+"F4.wireOp",EDGE,"E52.MirrorCS")])]});
            var Q112;
            Q112=makeQuery(id+"F5.opExtrude","SWEPT_EDGE",EDGE,{"disambiguationData":[OSD([sQuery(id+"F4.wireOp",EDGE,"E52.MirrorCS"),sQuery(id+"F4.wireOp",EDGE,"E54.MirrorCS")])]});
            var Q113;
            Q113=makeQuery(id+"F5.opExtrude","SWEPT_EDGE",EDGE,{"disambiguationData":[OSD([sQuery(id+"F4.wireOp",EDGE,"E11.top"),sQuery(id+"F4.wireOp",EDGE,"E11.right")])]});
            var Q114;
            Q114=makeQuery(id+"F5.opExtrude","SWEPT_EDGE",EDGE,{"disambiguationData":[OSD([sQuery(id+"F4.wireOp",EDGE,"E12.MirrorCS"),sQuery(id+"F4.wireOp",EDGE,"E14.MirrorCS")])]});
            var Q115;
            Q115=makeQuery(id+"F5.opExtrude","SWEPT_EDGE",EDGE,{"disambiguationData":[OSD([sQuery(id+"F4.wireOp",EDGE,"E17.MirrorCS"),sQuery(id+"F4.wireOp",EDGE,"E18.MirrorCS")])]});
            var Q116;
            Q116=makeQuery(id+"F5.opExtrude","SWEPT_EDGE",EDGE,{"disambiguationData":[OSD([sQuery(id+"F4.wireOp",EDGE,"E21.MirrorCS"),sQuery(id+"F4.wireOp",EDGE,"E22.MirrorCS")])]});
            var Q117;
            Q117=makeQuery(id+"F5.opExtrude","SWEPT_EDGE",EDGE,{"disambiguationData":[OSD([sQuery(id+"F4.wireOp",EDGE,"E25.MirrorCS"),sQuery(id+"F4.wireOp",EDGE,"E26.MirrorCS")])]});
            var Q118;
            Q118=makeQuery(id+"F5.opExtrude","SWEPT_EDGE",EDGE,{"disambiguationData":[OSD([sQuery(id+"F4.wireOp",EDGE,"E28.MirrorCS"),sQuery(id+"F4.wireOp",EDGE,"E31.MirrorCS")])]});
            var Q119;
            Q119=makeQuery(id+"F5.opExtrude","SWEPT_EDGE",EDGE,{"disambiguationData":[OSD([sQuery(id+"F4.wireOp",EDGE,"E30.MirrorCS"),sQuery(id+"F4.wireOp",EDGE,"E31.MirrorCS")])]});
            var Q120;
            Q120=makeQuery(id+"F5.opExtrude","SWEPT_EDGE",EDGE,{"disambiguationData":[OSD([sQuery(id+"F4.wireOp",EDGE,"E34.MirrorCS"),sQuery(id+"F4.wireOp",EDGE,"E35.MirrorCS")])]});
            var Q121;
            Q121=makeQuery(id+"F5.opExtrude","SWEPT_EDGE",EDGE,{"disambiguationData":[OSD([sQuery(id+"F4.wireOp",EDGE,"E33.MirrorCS"),sQuery(id+"F4.wireOp",EDGE,"E34.MirrorCS")])]});
            var Q122;
            Q122=makeQuery(id+"F5.opExtrude","CAP_EDGE",EDGE,{"disambiguationData":[OSD([sQuery(id+"F4.wireOp",EDGE,"E13.MirrorCS")])],"isStart":true});
            var Q123;
            Q123=makeQuery(id+"F5.opExtrude","SWEPT_EDGE",EDGE,{"disambiguationData":[OSD([sQuery(id+"F4.wireOp",EDGE,"E26.MirrorCS"),sQuery(id+"F4.wireOp",EDGE,"E27.MirrorCS")])]});
            var Q124;
            Q124=makeQuery(id+"F5.opExtrude","SWEPT_EDGE",EDGE,{"disambiguationData":[OSD([sQuery(id+"F4.wireOp",EDGE,"E22.MirrorCS"),sQuery(id+"F4.wireOp",EDGE,"E23.MirrorCS")])]});
            var Q125;
            Q125=makeQuery(id+"F5.opExtrude","SWEPT_EDGE",EDGE,{"disambiguationData":[OSD([sQuery(id+"F4.wireOp",EDGE,"E18.MirrorCS"),sQuery(id+"F4.wireOp",EDGE,"E19.MirrorCS")])]});
            var Q126;
            Q126=makeQuery(id+"F5.opExtrude","SWEPT_EDGE",EDGE,{"disambiguationData":[OSD([sQuery(id+"F4.wireOp",EDGE,"E14.MirrorCS"),sQuery(id+"F4.wireOp",EDGE,"E15.MirrorCS")])]});
            fillet(context, id + "F6", {"entities" : qUnion([Q0, Q1, Q2, Q3, Q4, Q5, Q6, Q7, Q8, Q9, Q10, Q11, Q12, Q13, Q14, Q15, Q16, Q17, Q18, Q19, Q20, Q21, Q22, Q23, Q24, Q25, Q26, Q27, Q28, Q29, Q30, Q31, Q32, Q33, Q34, Q35, Q36, Q37, Q38, Q39, Q40, Q41, Q42, Q43, Q44, Q45, Q46, Q47, Q48, Q49, Q50, Q51, Q52, Q53, Q54, Q55, Q56, Q57, Q58, Q59, Q60, Q61, Q62, Q63, Q64, Q65, Q66, Q67, Q68, Q69, Q70, Q71, Q72, Q73, Q74, Q75, Q76, Q77, Q78, Q79, Q80, Q81, Q82, Q83, Q84, Q85, Q86, Q87, Q88, Q89, Q90, Q91, Q92, Q93, Q94, Q95, Q96, Q97, Q98, Q99, Q100, Q101, Q102, Q103, Q104, Q105, Q106, Q107, Q108, Q109, Q110, Q111, Q112, Q113, Q114, Q115, Q116, Q117, Q118, Q119, Q120, Q121, Q122, Q123, Q124, Q125, Q126]), "radius" : 1 * mm, "allowEdgeOverflow" : false});
        }
        {
            var Q0;
            Q0=makeQuery(id+"F1.opRevolve","SWEPT_BODY",BODY,{"disambiguationData":[OSD([sQuery(id+"F0.wireOp",EDGE,"E1"),sQuery(id+"F0.wireOp",EDGE,"E2"),sQuery(id+"F0.wireOp",EDGE,"E3"),sQuery(id+"F0.wireOp",EDGE,"E4"),sQuery(id+"F0.wireOp",EDGE,"E5"),sQuery(id+"F0.wireOp",EDGE,"E6"),sQuery(id+"F0.wireOp",EDGE,"E7"),sQuery(id+"F0.wireOp",EDGE,"E8"),sQuery(id+"F0.wireOp",EDGE,"E9"),sQuery(id+"F0.wireOp",EDGE,"E10")])]});
            var Q1;
            Q1=sQuery(id+"F0.wireOp",EDGE,"E0");
            circularPattern(context, id + "F7", {"entities" : qUnion([Q0]), "axis" : qUnion([Q1]), "angle" : 360 * degree, "instanceCount" : 10, "equalSpace" : true});
        }
    });
